# Revit family: Ladder_Incline-Ship_UPNOVR_U-503
name_source: partatom
category: Generic Models
revit_build: Autodesk Revit Architecture 2012 (Build: 20110309_2315(x64)
units: mm (PartAtom-declared; Revit-internal decimal feet)

## types (1)
- As Specified
    Assembly Code = E1090900
    Capacity = 500 lbs per rung
    Default Elevation = 4' - 0"
    Description = UPNOVR U-503 Crossover with Platform Aluminum Ships Ladder
    Expected Lifespan (Years) = 0
    Foot CL Inset = 0' - 3 1/2"
    Frame Material = Metal - UPNOVR - 6061-T6 Aluminum
    Green Building-LEED = http://www.arcat.com
    Keynote = 05510
    Maintenance Schedule (Months) = 0
    Manufacturer = UPNOVR, Inc.
    Manufacturer Website = http://www.aclindustries.com
    Model = U-503
    Product Data = http://www.arcat.com
    Revision = R1_04-2013
    Sales Information = http://www.aclindustries.com
    Send Message = http://www.arcat.com
    Standards Conformance = OSHA and ANSI A14.3
    URL = http://www.aclindustries.com
    Unit Width = 2' - 0"
    Warranty Duration (Years) = 0
    handrailradi = 0' - 3"

## geometry (parser evidence)
native form markers: Blend x2, Sweep x8
no freeform markers — native parametric forms only
